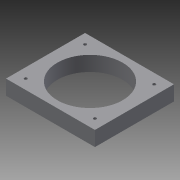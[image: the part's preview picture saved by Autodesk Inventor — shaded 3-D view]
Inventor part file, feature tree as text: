
AUTODESK INVENTOR PART (.ipt)
format: ipt  version: 2013 (Build 170138000, 138)  size: 92,160 bytes
history: native  units: mm
features: sketch x2, other x1, extrude x1, hole x1
ambient origin geometry x8: Origin, YZ Plane, XZ Plane, XY Plane, X Axis, Y Axis, Z Axis, Center Point
feature tree (5):
  other  "ソリッド1"
  extrude  "押し出し1"  Depth=80.0mm
  hole  "穴1"  [1 undecoded]
  sketch  "スケッチ1"
  sketch  "スケッチ2"
note: 1 required parameter value undecoded (feature->parameter linkage not recoverable at this tier; creation-order binding heuristic only, values carry confidence <= 0.55)
